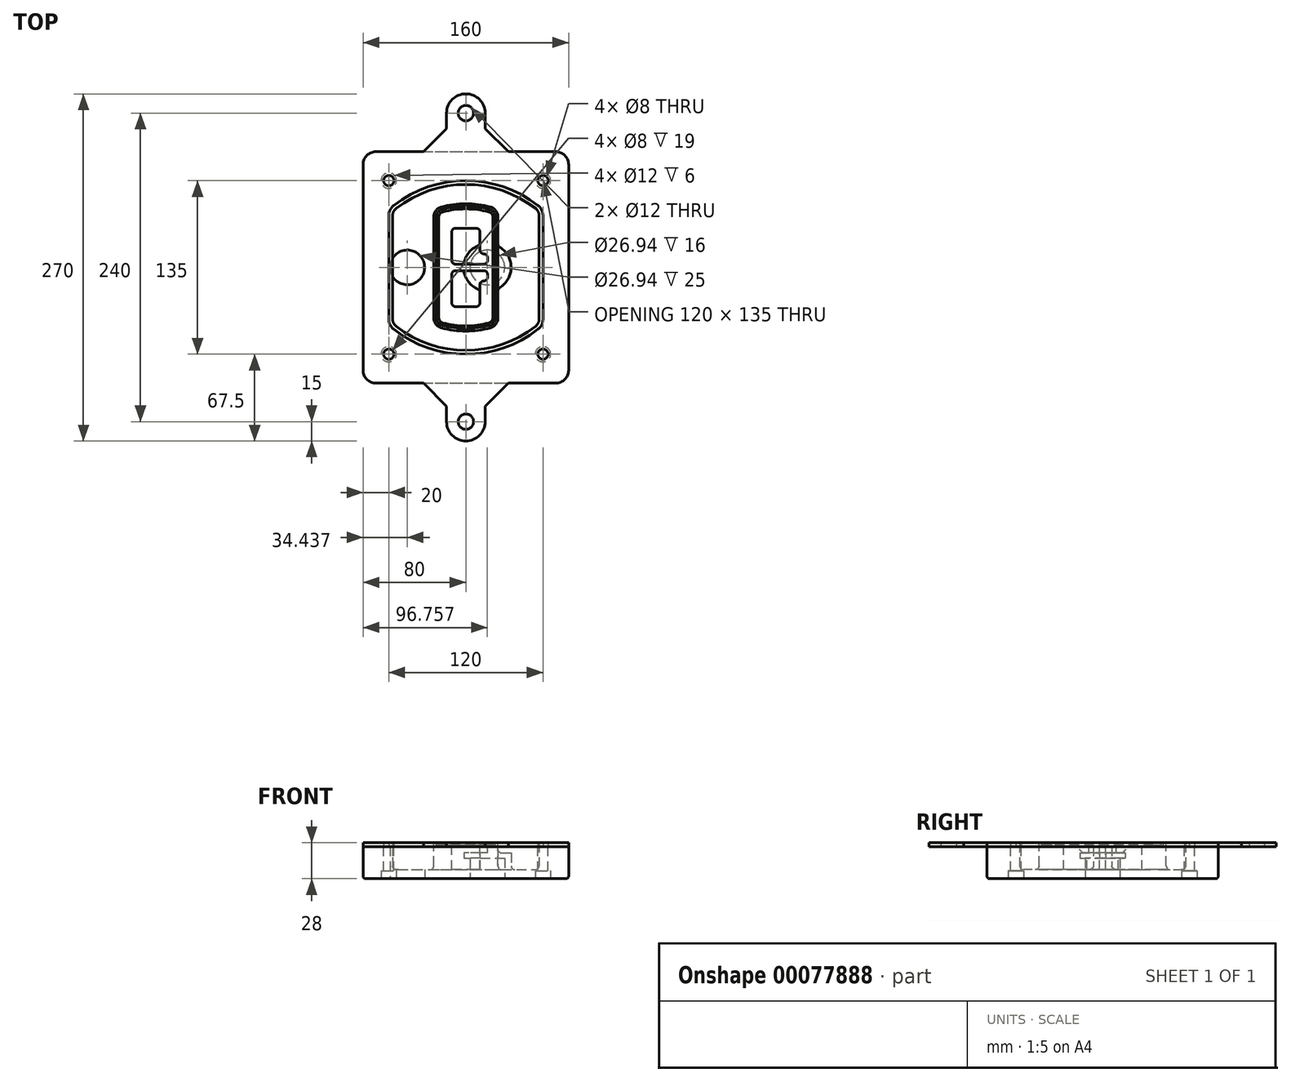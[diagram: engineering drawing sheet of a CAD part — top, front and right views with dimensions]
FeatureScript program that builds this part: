
annotation { "Feature Type Name" : "Feature", "Feature Type Description" : "" }
export const myFeature = defineFeature(function(context is Context, id is Id, definition is map)
    precondition{}
    {
        {
            var Q0;
            Q0=qCreatedBy(makeId("Top.planeOp"),FACE);
            var sketch = newSketch(context, id + "F0", { "sketchPlane" : qUnion([Q0])});
            skPoint(sketch, "E0.rect.middle", {"position": v(0, 0) * mm});
            skLineSegment(sketch, "E1.bottom", {"start": v(-70, -90) * mm, "end": v(70, -90) * mm});
            skLineSegment(sketch, "E1.top", {"start": v(-70, 90) * mm, "end": v(70, 90) * mm});
            skLineSegment(sketch, "E1.left", {"start": v(-80, -80) * mm, "end": v(-80, 80) * mm});
            skLineSegment(sketch, "E1.right", {"start": v(80, -80) * mm, "end": v(80, 80) * mm});
            skLineSegment(sketch, "E2", {"start": v(-80, 90) * mm, "end": v(80, -90) * mm, "construction": true});
            skLineSegment(sketch, "E3", {"start": v(80, 90) * mm, "end": v(-80, -90) * mm, "construction": true});
            skCircle(sketch, "E4", {"center": v(-60, 67.5) * mm, "radius": 4 * mm});
            skCircle(sketch, "E5", {"center": v(60, 67.5) * mm, "radius": 4 * mm});
            skCircle(sketch, "E6", {"center": v(60, -67.5) * mm, "radius": 4 * mm});
            skCircle(sketch, "E7", {"center": v(-60, -67.5) * mm, "radius": 4 * mm});
            skLineSegment(sketch, "E8", {"start": v(-60, 67.5) * mm, "end": v(60, 67.5) * mm, "construction": true});
            skLineSegment(sketch, "E9", {"start": v(60, 67.5) * mm, "end": v(60, -67.5) * mm, "construction": true});
            skLineSegment(sketch, "E10", {"start": v(60, -67.5) * mm, "end": v(-60, -67.5) * mm, "construction": true});
            skLineSegment(sketch, "E11", {"start": v(-60, -67.5) * mm, "end": v(-60, 67.5) * mm, "construction": true});
            skLineSegment(sketch, "E12", {"start": v(-60, 40.3) * mm, "end": v(-60, -40.3) * mm});
            skLineSegment(sketch, "E13", {"start": v(60, 40.3) * mm, "end": v(60, -40.3) * mm});
            skArc(sketch, "E14", {"start": v(56.15, 48.18) * mm, "mid": v(0, 67.5) * mm, "end": v(-56.15, 48.18) * mm});
            skArc(sketch, "E15", {"start": v(-56.15, -48.18) * mm, "mid": v(0, -67.5) * mm, "end": v(56.15, -48.18) * mm});
            skLineSegment(sketch, "E16", {"start": v(-60, 0) * mm, "end": v(60, 0) * mm, "construction": true});
            skPoint(sketch, "E17.visualSharp", {"position": v(-60, -45) * mm});
            skArc(sketch, "E17.filletArc", {"start": v(-60, -40.3) * mm, "mid": v(-58.99, -44.68) * mm, "end": v(-56.15, -48.18) * mm});
            skPoint(sketch, "E18.visualSharp", {"position": v(-60, 45) * mm});
            skArc(sketch, "E18.filletArc", {"start": v(-56.15, 48.18) * mm, "mid": v(-58.99, 44.68) * mm, "end": v(-60, 40.3) * mm});
            skPoint(sketch, "E19.visualSharp", {"position": v(60, 45) * mm});
            skArc(sketch, "E19.filletArc", {"start": v(60, 40.3) * mm, "mid": v(58.99, 44.68) * mm, "end": v(56.15, 48.18) * mm});
            skPoint(sketch, "E20.visualSharp", {"position": v(60, -45) * mm});
            skArc(sketch, "E20.filletArc", {"start": v(56.15, -48.18) * mm, "mid": v(58.99, -44.68) * mm, "end": v(60, -40.3) * mm});
            skPoint(sketch, "E21.visualSharp", {"position": v(-80, 90) * mm});
            skArc(sketch, "E21.filletArc", {"start": v(-70, 90) * mm, "mid": v(-77.07, 87.07) * mm, "end": v(-80, 80) * mm});
            skPoint(sketch, "E22.visualSharp", {"position": v(80, 90) * mm});
            skArc(sketch, "E22.filletArc", {"start": v(80, 80) * mm, "mid": v(77.07, 87.07) * mm, "end": v(70, 90) * mm});
            skPoint(sketch, "E23.visualSharp", {"position": v(80, -90) * mm});
            skArc(sketch, "E23.filletArc", {"start": v(70, -90) * mm, "mid": v(77.07, -87.07) * mm, "end": v(80, -80) * mm});
            skPoint(sketch, "E24.visualSharp", {"position": v(-80, -90) * mm});
            skArc(sketch, "E24.filletArc", {"start": v(-80, -80) * mm, "mid": v(-77.07, -87.07) * mm, "end": v(-70, -90) * mm});
            skArc(sketch, "E25.0", {"start": v(57, 40.3) * mm, "mid": v(56.3, 43.36) * mm, "end": v(54.3, 45.81) * mm});
            skLineSegment(sketch, "E25.1", {"start": v(57, 40.3) * mm, "end": v(57, -40.3) * mm});
            skArc(sketch, "E25.2", {"start": v(54.3, -45.81) * mm, "mid": v(56.3, -43.36) * mm, "end": v(57, -40.3) * mm});
            skArc(sketch, "E25.3", {"start": v(-54.3, -45.81) * mm, "mid": v(0, -64.5) * mm, "end": v(54.3, -45.81) * mm});
            skArc(sketch, "E25.4", {"start": v(-57, -40.3) * mm, "mid": v(-56.3, -43.36) * mm, "end": v(-54.3, -45.81) * mm});
            skArc(sketch, "E25.5", {"start": v(54.3, 45.81) * mm, "mid": v(0, 64.5) * mm, "end": v(-54.3, 45.81) * mm});
            skLineSegment(sketch, "E25.6", {"start": v(-57, 40.3) * mm, "end": v(-57, -40.3) * mm});
            skArc(sketch, "E25.7", {"start": v(-54.3, 45.81) * mm, "mid": v(-56.3, 43.36) * mm, "end": v(-57, 40.3) * mm});
            skArc(sketch, "E26.0", {"start": v(-58.62, 51.33) * mm, "mid": v(-62.58, 46.43) * mm, "end": v(-64, 40.3) * mm});
            skArc(sketch, "E26.1", {"start": v(58.62, 51.33) * mm, "mid": v(0, 71.5) * mm, "end": v(-58.62, 51.33) * mm});
            skArc(sketch, "E26.2", {"start": v(64, 40.3) * mm, "mid": v(62.58, 46.43) * mm, "end": v(58.62, 51.33) * mm});
            skLineSegment(sketch, "E26.3", {"start": v(64, 40.3) * mm, "end": v(64, -40.3) * mm});
            skArc(sketch, "E26.4", {"start": v(58.62, -51.33) * mm, "mid": v(62.58, -46.43) * mm, "end": v(64, -40.3) * mm});
            skLineSegment(sketch, "E26.5", {"start": v(-64, 40.3) * mm, "end": v(-64, -40.3) * mm});
            skArc(sketch, "E26.6", {"start": v(-58.62, -51.33) * mm, "mid": v(0, -71.5) * mm, "end": v(58.62, -51.33) * mm});
            skArc(sketch, "E26.7", {"start": v(-64, -40.3) * mm, "mid": v(-62.58, -46.43) * mm, "end": v(-58.62, -51.33) * mm});
            skSolve(sketch);
        }
        {
            var Q0;
            Q0=makeQuery(id+"F0.imprint","IMPRINT",FACE,{"disambiguationData":[TD([[makeQuery(id+"F0.imprint","IMPRINT",EDGE,{"derivedFrom":sQuery(id+"F0.wireOp",EDGE,"E1.bottom")}),1.0]])]});
            var Q1;
            Q1=makeQuery(id+"F0.imprint","IMPRINT",FACE,{"disambiguationData":[TD([[makeQuery(id+"F0.imprint","IMPRINT",EDGE,{"derivedFrom":sQuery(id+"F0.wireOp",EDGE,"E12")}),1.0]])]});
            var Q2;
            Q2=makeQuery(id+"F0.imprint","IMPRINT",FACE,{"disambiguationData":[TD([[makeQuery(id+"F0.imprint","IMPRINT",EDGE,{"derivedFrom":sQuery(id+"F0.wireOp",EDGE,"E25.0")}),1.0]])]});
            var Q3;
            Q3=makeQuery(id+"F0.imprint","IMPRINT",FACE,{"disambiguationData":[TD([[makeQuery(id+"F0.imprint","IMPRINT",EDGE,{"derivedFrom":sQuery(id+"F0.wireOp",EDGE,"E12")}),-1.0]])]});
            extrude(context, id + "F1", {"entities" : qUnion([Q0, Q1, Q2, Q3]), "oppositeDirection" : true, "depth" : 25 * mm});
        }
        {
            var Q0;
            Q0=makeQuery(id+"F0.imprint","IMPRINT",FACE,{"disambiguationData":[TD([[makeQuery(id+"F0.imprint","IMPRINT",EDGE,{"derivedFrom":sQuery(id+"F0.wireOp",EDGE,"E12")}),1.0]])]});
            extrude(context, id + "F2", {"entities" : qUnion([Q0]), "operationType" : NewBodyOperationType.ADD, "depth" : 3 * mm});
        }
        {
            var Q0;
            Q0=makeQuery(id+"F0.imprint","IMPRINT",FACE,{"disambiguationData":[TD([[makeQuery(id+"F0.imprint","IMPRINT",EDGE,{"derivedFrom":sQuery(id+"F0.wireOp",EDGE,"E25.0")}),1.0]])]});
            extrude(context, id + "F3", {"entities" : qUnion([Q0]), "operationType" : NewBodyOperationType.REMOVE, "oppositeDirection" : true, "depth" : 18 * mm});
        }
        {
            var Q0;
            Q0=makeQuery(id+"F2.opExtrude","CAP_FACE",FACE,{"disambiguationData":[OSD([sQuery(id+"F0.wireOp",EDGE,"E12"),sQuery(id+"F0.wireOp",EDGE,"E13"),sQuery(id+"F0.wireOp",EDGE,"E14"),sQuery(id+"F0.wireOp",EDGE,"E15"),sQuery(id+"F0.wireOp",EDGE,"E17.filletArc"),sQuery(id+"F0.wireOp",EDGE,"E18.filletArc"),sQuery(id+"F0.wireOp",EDGE,"E19.filletArc"),sQuery(id+"F0.wireOp",EDGE,"E20.filletArc"),sQuery(id+"F0.wireOp",EDGE,"E25.0"),sQuery(id+"F0.wireOp",EDGE,"E25.1"),sQuery(id+"F0.wireOp",EDGE,"E25.2"),sQuery(id+"F0.wireOp",EDGE,"E25.3"),sQuery(id+"F0.wireOp",EDGE,"E25.4"),sQuery(id+"F0.wireOp",EDGE,"E25.5"),sQuery(id+"F0.wireOp",EDGE,"E25.6"),sQuery(id+"F0.wireOp",EDGE,"E25.7")])],"isStart":false});
            var sketch = newSketch(context, id + "F4", { "sketchPlane" : qUnion([Q0])});
            skArc(sketch, "E27.0", {"start": v(-19.08, -46.97) * mm, "mid": v(0, -49.5) * mm, "end": v(19.08, -46.97) * mm});
            skArc(sketch, "E28.0", {"start": v(19.08, 46.97) * mm, "mid": v(0, 49.5) * mm, "end": v(-19.08, 46.97) * mm});
            skLineSegment(sketch, "E29", {"start": v(-25, 39.25) * mm, "end": v(-25, -39.25) * mm});
            skLineSegment(sketch, "E30", {"start": v(25, 39.25) * mm, "end": v(25, -39.25) * mm});
            skLineSegment(sketch, "E31", {"start": v(-25, 45.1) * mm, "end": v(25, 45.1) * mm, "construction": true});
            skLineSegment(sketch, "E32", {"start": v(-25, -45.1) * mm, "end": v(25, -45.1) * mm, "construction": true});
            skPoint(sketch, "E33.visualSharp", {"position": v(-25, 45.1) * mm});
            skArc(sketch, "E33.filletArc", {"start": v(-19.08, 46.97) * mm, "mid": v(-23.35, 44.11) * mm, "end": v(-25, 39.25) * mm});
            skPoint(sketch, "E34.visualSharp", {"position": v(25, 45.1) * mm});
            skArc(sketch, "E34.filletArc", {"start": v(25, 39.25) * mm, "mid": v(23.35, 44.11) * mm, "end": v(19.08, 46.97) * mm});
            skPoint(sketch, "E35.visualSharp", {"position": v(25, -45.1) * mm});
            skArc(sketch, "E35.filletArc", {"start": v(19.08, -46.97) * mm, "mid": v(23.35, -44.11) * mm, "end": v(25, -39.25) * mm});
            skPoint(sketch, "E36.visualSharp", {"position": v(-25, -45.1) * mm});
            skArc(sketch, "E36.filletArc", {"start": v(-25, -39.25) * mm, "mid": v(-23.35, -44.11) * mm, "end": v(-19.08, -46.97) * mm});
            skArc(sketch, "E37.0", {"start": v(54.3, 45.81) * mm, "mid": v(0, 64.5) * mm, "end": v(-54.3, 45.81) * mm});
            skArc(sketch, "E37.1", {"start": v(-54.3, 45.81) * mm, "mid": v(-56.3, 43.36) * mm, "end": v(-57, 40.3) * mm});
            skLineSegment(sketch, "E37.2", {"start": v(-57, 40.3) * mm, "end": v(-57, -40.3) * mm});
            skArc(sketch, "E37.3", {"start": v(-57, -40.3) * mm, "mid": v(-56.3, -43.36) * mm, "end": v(-54.3, -45.81) * mm});
            skArc(sketch, "E37.4", {"start": v(-54.3, -45.81) * mm, "mid": v(0, -64.5) * mm, "end": v(54.3, -45.81) * mm});
            skArc(sketch, "E37.5", {"start": v(54.3, -45.81) * mm, "mid": v(56.3, -43.36) * mm, "end": v(57, -40.3) * mm});
            skLineSegment(sketch, "E37.6", {"start": v(57, 40.3) * mm, "end": v(57, -40.3) * mm});
            skArc(sketch, "E37.7", {"start": v(57, 40.3) * mm, "mid": v(56.3, 43.36) * mm, "end": v(54.3, 45.81) * mm});
            skLineSegment(sketch, "E38.0", {"start": v(23, 39.25) * mm, "end": v(23, -39.25) * mm});
            skArc(sketch, "E38.1", {"start": v(18.56, -45.04) * mm, "mid": v(21.76, -42.9) * mm, "end": v(23, -39.25) * mm});
            skArc(sketch, "E38.2", {"start": v(-18.56, -45.04) * mm, "mid": v(0, -47.5) * mm, "end": v(18.56, -45.04) * mm});
            skArc(sketch, "E38.3", {"start": v(-23, -39.25) * mm, "mid": v(-21.76, -42.9) * mm, "end": v(-18.56, -45.04) * mm});
            skLineSegment(sketch, "E38.4", {"start": v(-23, 39.25) * mm, "end": v(-23, -39.25) * mm});
            skArc(sketch, "E38.5", {"start": v(23, 39.25) * mm, "mid": v(21.76, 42.9) * mm, "end": v(18.56, 45.04) * mm});
            skArc(sketch, "E38.6", {"start": v(-18.56, 45.04) * mm, "mid": v(-21.76, 42.9) * mm, "end": v(-23, 39.25) * mm});
            skArc(sketch, "E38.7", {"start": v(18.56, 45.04) * mm, "mid": v(0, 47.5) * mm, "end": v(-18.56, 45.04) * mm});
            skArc(sketch, "E39.0", {"start": v(21, 39.25) * mm, "mid": v(20.18, 41.68) * mm, "end": v(18.04, 43.1) * mm});
            skLineSegment(sketch, "E39.1", {"start": v(21, 39.25) * mm, "end": v(21, -39.25) * mm});
            skArc(sketch, "E39.2", {"start": v(18.04, -43.1) * mm, "mid": v(20.18, -41.68) * mm, "end": v(21, -39.25) * mm});
            skArc(sketch, "E39.3", {"start": v(-18.04, -43.1) * mm, "mid": v(0, -45.5) * mm, "end": v(18.04, -43.1) * mm});
            skArc(sketch, "E39.4", {"start": v(-21, -39.25) * mm, "mid": v(-20.18, -41.68) * mm, "end": v(-18.04, -43.1) * mm});
            skArc(sketch, "E39.5", {"start": v(18.04, 43.1) * mm, "mid": v(0, 45.5) * mm, "end": v(-18.04, 43.1) * mm});
            skLineSegment(sketch, "E39.6", {"start": v(-21, 39.25) * mm, "end": v(-21, -39.25) * mm});
            skArc(sketch, "E39.7", {"start": v(-18.04, 43.1) * mm, "mid": v(-20.18, 41.68) * mm, "end": v(-21, 39.25) * mm});
            skLineSegment(sketch, "E40", {"start": v(-25, 0) * mm, "end": v(25, 0) * mm, "construction": true});
            skLineSegment(sketch, "E41", {"start": v(-11, 5.5) * mm, "end": v(-11, 27.5) * mm});
            skLineSegment(sketch, "E42", {"start": v(-8, 30.5) * mm, "end": v(8, 30.5) * mm});
            skLineSegment(sketch, "E43", {"start": v(11, 27.5) * mm, "end": v(11, 13.5) * mm});
            skLineSegment(sketch, "E44", {"start": v(14, 10.5) * mm, "end": v(14, 10.5) * mm});
            skLineSegment(sketch, "E45", {"start": v(17, 7.5) * mm, "end": v(17, 5.5) * mm});
            skLineSegment(sketch, "E46", {"start": v(14, 2.5) * mm, "end": v(-8, 2.5) * mm});
            skPoint(sketch, "E47.visualSharp", {"position": v(-11, 30.5) * mm});
            skArc(sketch, "E47.filletArc", {"start": v(-8, 30.5) * mm, "mid": v(-10.12, 29.62) * mm, "end": v(-11, 27.5) * mm});
            skPoint(sketch, "E48.visualSharp", {"position": v(11, 30.5) * mm});
            skArc(sketch, "E48.filletArc", {"start": v(11, 27.5) * mm, "mid": v(10.12, 29.62) * mm, "end": v(8, 30.5) * mm});
            skPoint(sketch, "E49.visualSharp", {"position": v(11, 10.5) * mm});
            skArc(sketch, "E49.filletArc", {"start": v(11, 13.5) * mm, "mid": v(11.88, 11.38) * mm, "end": v(14, 10.5) * mm});
            skPoint(sketch, "E50.visualSharp", {"position": v(17, 10.5) * mm});
            skArc(sketch, "E50.filletArc", {"start": v(17, 7.5) * mm, "mid": v(16.12, 9.62) * mm, "end": v(14, 10.5) * mm});
            skPoint(sketch, "E51.visualSharp", {"position": v(17, 2.5) * mm});
            skArc(sketch, "E51.filletArc", {"start": v(14, 2.5) * mm, "mid": v(16.12, 3.38) * mm, "end": v(17, 5.5) * mm});
            skPoint(sketch, "E52.visualSharp", {"position": v(-11, 2.5) * mm});
            skArc(sketch, "E52.filletArc", {"start": v(-11, 5.5) * mm, "mid": v(-10.12, 3.38) * mm, "end": v(-8, 2.5) * mm});
            skLineSegment(sketch, "E53.0.MirrorCS", {"start": v(14, -2.5) * mm, "end": v(-8, -2.5) * mm});
            skArc(sketch, "E54.0.MirrorCS", {"start": v(-11, -5.5) * mm, "mid": v(-10.12, -3.38) * mm, "end": v(-8, -2.5) * mm});
            skLineSegment(sketch, "E55.0.MirrorCS", {"start": v(-11, -5.5) * mm, "end": v(-11, -27.5) * mm});
            skArc(sketch, "E56.0.MirrorCS", {"start": v(-8, -30.5) * mm, "mid": v(-10.12, -29.62) * mm, "end": v(-11, -27.5) * mm});
            skLineSegment(sketch, "E57.0.MirrorCS", {"start": v(-8, -30.5) * mm, "end": v(8, -30.5) * mm});
            skArc(sketch, "E58.0.MirrorCS", {"start": v(11, -27.5) * mm, "mid": v(10.12, -29.62) * mm, "end": v(8, -30.5) * mm});
            skLineSegment(sketch, "E59.0.MirrorCS", {"start": v(11, -27.5) * mm, "end": v(11, -13.5) * mm});
            skArc(sketch, "E60.0.MirrorCS", {"start": v(11, -13.5) * mm, "mid": v(11.88, -11.38) * mm, "end": v(14, -10.5) * mm});
            skArc(sketch, "E61.0.MirrorCS", {"start": v(17, -7.5) * mm, "mid": v(16.12, -9.62) * mm, "end": v(14, -10.5) * mm});
            skLineSegment(sketch, "E62.0.MirrorCS", {"start": v(17, -7.5) * mm, "end": v(17, -5.5) * mm});
            skArc(sketch, "E63.0.MirrorCS", {"start": v(14, -2.5) * mm, "mid": v(16.12, -3.38) * mm, "end": v(17, -5.5) * mm});
            skSolve(sketch);
        }
        {
            var Q0;
            Q0=makeQuery(id+"F4.imprint","IMPRINT",FACE,{"disambiguationData":[TD([[makeQuery(id+"F4.imprint","IMPRINT",EDGE,{"derivedFrom":sQuery(id+"F4.wireOp",EDGE,"E27.0")}),1.0]])]});
            var Q1;
            Q1=makeQuery(id+"F4.imprint","IMPRINT",FACE,{"disambiguationData":[TD([[makeQuery(id+"F4.imprint","IMPRINT",EDGE,{"derivedFrom":sQuery(id+"F4.wireOp",EDGE,"E38.0")}),-1.0]])]});
            var Q2;
            Q2=makeQuery(id+"F4.imprint","IMPRINT",FACE,{"disambiguationData":[TD([[makeQuery(id+"F4.imprint","IMPRINT",EDGE,{"derivedFrom":sQuery(id+"F4.wireOp",EDGE,"E39.0")}),1.0]])]});
            extrude(context, id + "F5", {"entities" : qUnion([Q0, Q1, Q2]), "operationType" : NewBodyOperationType.ADD, "endBound" : BoundingType.UP_TO_NEXT, "oppositeDirection" : true, "depth" : 25 * mm});
        }
        {
            var Q0;
            Q0=makeQuery(id+"F4.imprint","IMPRINT",FACE,{"disambiguationData":[TD([[makeQuery(id+"F4.imprint","IMPRINT",EDGE,{"derivedFrom":sQuery(id+"F4.wireOp",EDGE,"E38.0")}),-1.0]])]});
            extrude(context, id + "F6", {"entities" : qUnion([Q0]), "operationType" : NewBodyOperationType.REMOVE, "oppositeDirection" : true, "depth" : 2 * mm});
        }
        {
            var Q0;
            Q0=makeQuery(id+"F1.opExtrude","CAP_FACE",FACE,{"disambiguationData":[OSD([sQuery(id+"F0.wireOp",EDGE,"E1.bottom"),sQuery(id+"F0.wireOp",EDGE,"E1.top"),sQuery(id+"F0.wireOp",EDGE,"E1.left"),sQuery(id+"F0.wireOp",EDGE,"E1.right"),sQuery(id+"F0.wireOp",EDGE,"E4"),sQuery(id+"F0.wireOp",EDGE,"E5"),sQuery(id+"F0.wireOp",EDGE,"E6"),sQuery(id+"F0.wireOp",EDGE,"E7"),sQuery(id+"F0.wireOp",EDGE,"E21.filletArc"),sQuery(id+"F0.wireOp",EDGE,"E22.filletArc"),sQuery(id+"F0.wireOp",EDGE,"E23.filletArc"),sQuery(id+"F0.wireOp",EDGE,"E24.filletArc")])],"isStart":false});
            var sketch = newSketch(context, id + "F7", { "sketchPlane" : qUnion([Q0])});
            skCircle(sketch, "E64", {"center": v(16.76, 0) * mm, "radius": 13.47 * mm});
            skCircle(sketch, "E65", {"center": v(-45.56, 0) * mm, "radius": 13.47 * mm});
            skLineSegment(sketch, "E66", {"start": v(80, 0) * mm, "end": v(-80, 0) * mm});
            skCircle(sketch, "E67", {"center": v(16.76, 0) * mm, "radius": 18.47 * mm});
            skCircle(sketch, "E68", {"center": v(60, -67.5) * mm, "radius": 6 * mm});
            skCircle(sketch, "E69", {"center": v(-60, -67.5) * mm, "radius": 6 * mm});
            skCircle(sketch, "E70", {"center": v(-60, 67.5) * mm, "radius": 6 * mm});
            skCircle(sketch, "E71", {"center": v(60, 67.5) * mm, "radius": 6 * mm});
            skSolve(sketch);
        }
        {
            var Q0;
            {var subQ1=sQuery(id+"F7.wireOp",EDGE,"E66");var subQ4=sQuery(id+"F7.wireOp",EDGE,"E64");var subQ6=makeQuery(id+"F7.imprint","INTERSECT",VERTEX,{"disambiguationData":[OD(0.0)],"derivedFrom":[subQ4,subQ1]});Q0=makeQuery(id+"F7.imprint","IMPRINT",FACE,{"disambiguationData":[TD([[makeQuery(id+"F7.imprint","IMPRINT",EDGE,{"disambiguationData":[TD([[subQ6,-1.0]])],"derivedFrom":subQ4}),-1.0]])]});}
            var Q1;
            {var subQ0=sQuery(id+"F7.wireOp",EDGE,"E66");var subQ1=sQuery(id+"F7.wireOp",EDGE,"E64");var subQ3=makeQuery(id+"F7.imprint","INTERSECT",VERTEX,{"disambiguationData":[OD(0.0)],"derivedFrom":[subQ1,subQ0]});Q1=makeQuery(id+"F7.imprint","IMPRINT",FACE,{"disambiguationData":[TD([[makeQuery(id+"F7.imprint","IMPRINT",EDGE,{"disambiguationData":[TD([[subQ3,-1.0]])],"derivedFrom":subQ1}),1.0]])]});}
            var Q2;
            {var subQ0=sQuery(id+"F7.wireOp",EDGE,"E66");var subQ1=sQuery(id+"F7.wireOp",EDGE,"E64");var subQ3=makeQuery(id+"F7.imprint","INTERSECT",VERTEX,{"disambiguationData":[OD(0.0)],"derivedFrom":[subQ1,subQ0]});Q2=makeQuery(id+"F7.imprint","IMPRINT",FACE,{"disambiguationData":[TD([[makeQuery(id+"F7.imprint","IMPRINT",EDGE,{"disambiguationData":[TD([[subQ3,1.0]])],"derivedFrom":subQ1}),1.0]])]});}
            var Q3;
            {var subQ1=sQuery(id+"F7.wireOp",EDGE,"E66");var subQ4=sQuery(id+"F7.wireOp",EDGE,"E64");var subQ6=makeQuery(id+"F7.imprint","INTERSECT",VERTEX,{"disambiguationData":[OD(0.0)],"derivedFrom":[subQ4,subQ1]});Q3=makeQuery(id+"F7.imprint","IMPRINT",FACE,{"disambiguationData":[TD([[makeQuery(id+"F7.imprint","IMPRINT",EDGE,{"disambiguationData":[TD([[subQ6,1.0]])],"derivedFrom":subQ4}),-1.0]])]});}
            extrude(context, id + "F8", {"entities" : qUnion([Q0, Q1, Q2, Q3]), "operationType" : NewBodyOperationType.ADD, "oppositeDirection" : true, "depth" : 20 * mm});
        }
        {
            var Q0;
            {var subQ0=sQuery(id+"F7.wireOp",EDGE,"E66");var subQ1=sQuery(id+"F7.wireOp",EDGE,"E64");var subQ3=makeQuery(id+"F7.imprint","INTERSECT",VERTEX,{"disambiguationData":[OD(0.0)],"derivedFrom":[subQ1,subQ0]});Q0=makeQuery(id+"F7.imprint","IMPRINT",FACE,{"disambiguationData":[TD([[makeQuery(id+"F7.imprint","IMPRINT",EDGE,{"disambiguationData":[TD([[subQ3,-1.0]])],"derivedFrom":subQ1}),1.0]])]});}
            var Q1;
            {var subQ0=sQuery(id+"F7.wireOp",EDGE,"E66");var subQ1=sQuery(id+"F7.wireOp",EDGE,"E64");var subQ3=makeQuery(id+"F7.imprint","INTERSECT",VERTEX,{"disambiguationData":[OD(0.0)],"derivedFrom":[subQ1,subQ0]});Q1=makeQuery(id+"F7.imprint","IMPRINT",FACE,{"disambiguationData":[TD([[makeQuery(id+"F7.imprint","IMPRINT",EDGE,{"disambiguationData":[TD([[subQ3,1.0]])],"derivedFrom":subQ1}),1.0]])]});}
            extrude(context, id + "F9", {"entities" : qUnion([Q0, Q1]), "operationType" : NewBodyOperationType.REMOVE, "oppositeDirection" : true, "depth" : 16 * mm});
        }
        {
            var Q0;
            {var subQ0=sQuery(id+"F7.wireOp",EDGE,"E66");var subQ1=sQuery(id+"F7.wireOp",EDGE,"E65");var subQ3=makeQuery(id+"F7.imprint","INTERSECT",VERTEX,{"disambiguationData":[OD(0.0)],"derivedFrom":[subQ1,subQ0]});Q0=makeQuery(id+"F7.imprint","IMPRINT",FACE,{"disambiguationData":[TD([[makeQuery(id+"F7.imprint","IMPRINT",EDGE,{"disambiguationData":[TD([[subQ3,-1.0]])],"derivedFrom":subQ1}),1.0]])]});}
            var Q1;
            {var subQ0=sQuery(id+"F7.wireOp",EDGE,"E66");var subQ1=sQuery(id+"F7.wireOp",EDGE,"E65");var subQ3=makeQuery(id+"F7.imprint","INTERSECT",VERTEX,{"disambiguationData":[OD(0.0)],"derivedFrom":[subQ1,subQ0]});Q1=makeQuery(id+"F7.imprint","IMPRINT",FACE,{"disambiguationData":[TD([[makeQuery(id+"F7.imprint","IMPRINT",EDGE,{"disambiguationData":[TD([[subQ3,1.0]])],"derivedFrom":subQ1}),1.0]])]});}
            extrude(context, id + "F10", {"entities" : qUnion([Q0, Q1]), "operationType" : NewBodyOperationType.REMOVE, "oppositeDirection" : true, "depth" : 25 * mm});
        }
        {
            var Q0;
            Q0=makeQuery(id+"F7.imprint","IMPRINT",FACE,{"disambiguationData":[TD([[makeQuery(id+"F7.imprint","IMPRINT",EDGE,{"derivedFrom":sQuery(id+"F7.wireOp",EDGE,"E68")}),1.0]])]});
            var Q1;
            Q1=makeQuery(id+"F7.imprint","IMPRINT",FACE,{"disambiguationData":[TD([[makeQuery(id+"F7.imprint","IMPRINT",EDGE,{"derivedFrom":makeQuery(id+"F1.opExtrude","CAP_EDGE",EDGE,{"disambiguationData":[OSD([sQuery(id+"F0.wireOp",EDGE,"E5")])],"isStart":false})}),-1.0]])]});
            var Q2;
            Q2=makeQuery(id+"F7.imprint","IMPRINT",FACE,{"disambiguationData":[TD([[makeQuery(id+"F7.imprint","IMPRINT",EDGE,{"derivedFrom":sQuery(id+"F7.wireOp",EDGE,"E69")}),1.0]])]});
            var Q3;
            Q3=makeQuery(id+"F7.imprint","IMPRINT",FACE,{"disambiguationData":[TD([[makeQuery(id+"F7.imprint","IMPRINT",EDGE,{"derivedFrom":makeQuery(id+"F1.opExtrude","CAP_EDGE",EDGE,{"disambiguationData":[OSD([sQuery(id+"F0.wireOp",EDGE,"E4")])],"isStart":false})}),-1.0]])]});
            var Q4;
            Q4=makeQuery(id+"F7.imprint","IMPRINT",FACE,{"disambiguationData":[TD([[makeQuery(id+"F7.imprint","IMPRINT",EDGE,{"derivedFrom":sQuery(id+"F7.wireOp",EDGE,"E70")}),1.0]])]});
            var Q5;
            Q5=makeQuery(id+"F7.imprint","IMPRINT",FACE,{"disambiguationData":[TD([[makeQuery(id+"F7.imprint","IMPRINT",EDGE,{"derivedFrom":makeQuery(id+"F1.opExtrude","CAP_EDGE",EDGE,{"disambiguationData":[OSD([sQuery(id+"F0.wireOp",EDGE,"E7")])],"isStart":false})}),-1.0]])]});
            var Q6;
            Q6=makeQuery(id+"F7.imprint","IMPRINT",FACE,{"disambiguationData":[TD([[makeQuery(id+"F7.imprint","IMPRINT",EDGE,{"derivedFrom":sQuery(id+"F7.wireOp",EDGE,"E71")}),1.0]])]});
            var Q7;
            Q7=makeQuery(id+"F7.imprint","IMPRINT",FACE,{"disambiguationData":[TD([[makeQuery(id+"F7.imprint","IMPRINT",EDGE,{"derivedFrom":makeQuery(id+"F1.opExtrude","CAP_EDGE",EDGE,{"disambiguationData":[OSD([sQuery(id+"F0.wireOp",EDGE,"E6")])],"isStart":false})}),-1.0]])]});
            extrude(context, id + "F11", {"entities" : qUnion([Q0, Q1, Q2, Q3, Q4, Q5, Q6, Q7]), "operationType" : NewBodyOperationType.REMOVE, "oppositeDirection" : true, "depth" : 6 * mm});
        }
        {
            var Q0;
            Q0=makeQuery(id+"F9.boolean.opBoolean","COPY",FACE,{"derivedFrom":makeQuery(id+"F9.opExtrude","CAP_FACE",FACE,{"disambiguationData":[OSD([sQuery(id+"F7.wireOp",EDGE,"E64")])],"isStart":false})});
            var sketch = newSketch(context, id + "F12", { "sketchPlane" : qUnion([Q0])});
            skArc(sketch, "E72.0", {"start": v(11, 17.55) * mm, "mid": v(2.57, 11.82) * mm, "end": v(-1.54, 2.5) * mm});
            skArc(sketch, "E72.1", {"start": v(-1.54, -2.5) * mm, "mid": v(2.57, -11.82) * mm, "end": v(11, -17.55) * mm});
            skLineSegment(sketch, "E73", {"start": v(-1.54, -2.5) * mm, "end": v(14, -2.5) * mm});
            skLineSegment(sketch, "E74.0", {"start": v(14, 2.5) * mm, "end": v(-1.54, 2.5) * mm});
            skArc(sketch, "E74.1", {"start": v(14, 2.5) * mm, "mid": v(16.12, 3.38) * mm, "end": v(17, 5.5) * mm});
            skLineSegment(sketch, "E74.2", {"start": v(17, 7.5) * mm, "end": v(17, 5.5) * mm});
            skArc(sketch, "E74.3", {"start": v(17, 7.5) * mm, "mid": v(16.12, 9.62) * mm, "end": v(14, 10.5) * mm});
            skArc(sketch, "E74.4", {"start": v(11, 13.5) * mm, "mid": v(11.88, 11.38) * mm, "end": v(14, 10.5) * mm});
            skLineSegment(sketch, "E74.5", {"start": v(11, 17.55) * mm, "end": v(11, 13.5) * mm});
            skLineSegment(sketch, "E74.7", {"start": v(14, -2.5) * mm, "end": v(-1.54, -2.5) * mm});
            skArc(sketch, "E74.8", {"start": v(14, -2.5) * mm, "mid": v(16.12, -3.38) * mm, "end": v(17, -5.5) * mm});
            skLineSegment(sketch, "E74.9", {"start": v(17, -7.5) * mm, "end": v(17, -5.5) * mm});
            skArc(sketch, "E74.10", {"start": v(17, -7.5) * mm, "mid": v(16.12, -9.62) * mm, "end": v(14, -10.5) * mm});
            skArc(sketch, "E74.11", {"start": v(11, -13.5) * mm, "mid": v(11.88, -11.38) * mm, "end": v(14, -10.5) * mm});
            skLineSegment(sketch, "E74.12", {"start": v(11, -17.55) * mm, "end": v(11, -13.5) * mm});
            skPoint(sketch, "E75.orphan", {"position": v(11, -27.5) * mm});
            skPoint(sketch, "E76.orphan", {"position": v(-8, -2.5) * mm});
            skPoint(sketch, "E77.orphan", {"position": v(-8, 2.5) * mm});
            skPoint(sketch, "E78.orphan", {"position": v(11, 27.5) * mm});
            skSolve(sketch);
        }
        {
            var Q0;
            {var subQ7=sQuery(id+"F12.wireOp",EDGE,"E72.0");var subQ14=sQuery(id+"F12.wireOp",EDGE,"E72.1");var subQ16=sQuery(id+"F12.wireOp",EDGE,"E74.1");var subQ18=sQuery(id+"F12.wireOp",EDGE,"E74.8");Q0=qUnion([makeQuery(id+"F12.imprint","IMPRINT",FACE,{"disambiguationData":[TD([[makeQuery(id+"F12.imprint","IMPRINT",EDGE,{"derivedFrom":subQ7}),1.0]])]}),makeQuery(id+"F12.imprint","IMPRINT",FACE,{"disambiguationData":[TD([[makeQuery(id+"F12.imprint","IMPRINT",EDGE,{"derivedFrom":subQ14}),1.0]])]}),makeQuery(id+"F12.imprint","IMPRINT",FACE,{"disambiguationData":[TD([[makeQuery(id+"F12.imprint","IMPRINT",EDGE,{"derivedFrom":subQ16}),1.0]])]}),makeQuery(id+"F12.imprint","IMPRINT",FACE,{"disambiguationData":[TD([[makeQuery(id+"F12.imprint","IMPRINT",EDGE,{"derivedFrom":subQ18}),-1.0]])]})]);}
            var Q1;
            Q1=makeQuery(id+"F5.boolean.opBoolean","SPLIT",FACE,{"disambiguationData":[TD([makeQuery(id+"F5.opExtrude","SWEPT_FACE",FACE,{"disambiguationData":[OSD([sQuery(id+"F4.wireOp",EDGE,"E41")])]})])],"derivedFrom":makeQuery(id+"F3.boolean.opBoolean","COPY",FACE,{"derivedFrom":makeQuery(id+"F3.opExtrude","CAP_FACE",FACE,{"disambiguationData":[OSD([sQuery(id+"F0.wireOp",EDGE,"E25.0"),sQuery(id+"F0.wireOp",EDGE,"E25.1"),sQuery(id+"F0.wireOp",EDGE,"E25.2"),sQuery(id+"F0.wireOp",EDGE,"E25.3"),sQuery(id+"F0.wireOp",EDGE,"E25.4"),sQuery(id+"F0.wireOp",EDGE,"E25.5"),sQuery(id+"F0.wireOp",EDGE,"E25.6"),sQuery(id+"F0.wireOp",EDGE,"E25.7")])],"isStart":false})})});
            extrude(context, id + "F13", {"entities" : qUnion([Q0]), "operationType" : NewBodyOperationType.REMOVE, "endBound" : BoundingType.UP_TO_SURFACE, "endBoundEntityFace" : qUnion([Q1]), "depth" : 25 * mm});
        }
        {
            var Q0;
            Q0=makeQuery(id+"F3.boolean.opBoolean","COPY",EDGE,{"derivedFrom":makeQuery(id+"F3.opExtrude","CAP_EDGE",EDGE,{"disambiguationData":[OSD([sQuery(id+"F0.wireOp",EDGE,"E25.6")])],"isStart":false})});
            var Q1;
            Q1=makeQuery(id+"F8.boolean.opBoolean","INTERSECT",EDGE,{"derivedFrom":[makeQuery(id+"F5.opExtrude","SWEPT_FACE",FACE,{"disambiguationData":[OSD([sQuery(id+"F4.wireOp",EDGE,"E30")])]}),makeQuery(id+"F8.opExtrude","CAP_FACE",FACE,{"disambiguationData":[OSD([sQuery(id+"F7.wireOp",EDGE,"E67")])],"isStart":false})]});
            var Q2;
            Q2=makeQuery(id+"F8.boolean.opBoolean","INTERSECT",EDGE,{"disambiguationData":[OD(1.0)],"derivedFrom":[makeQuery(id+"F5.opExtrude","SWEPT_FACE",FACE,{"disambiguationData":[OSD([sQuery(id+"F4.wireOp",EDGE,"E30")])]}),makeQuery(id+"F8.opExtrude","SWEPT_FACE",FACE,{"disambiguationData":[OSD([sQuery(id+"F7.wireOp",EDGE,"E67")])]})]});
            var Q3;
            {var subQ0=sQuery(id+"F4.wireOp",EDGE,"E30");Q3=makeQuery(id+"F8.boolean.opBoolean","SPLIT",EDGE,{"disambiguationData":[TD([makeQuery(id+"F5.opExtrude","SWEPT_FACE",FACE,{"disambiguationData":[OSD([sQuery(id+"F4.wireOp",EDGE,"E35.filletArc")])]})])],"derivedFrom":makeQuery(id+"F5.opExtrude","CAP_EDGE",EDGE,{"disambiguationData":[OSD([subQ0])],"isStart":false})});}
            var Q4;
            {var subQ0=sQuery(id+"F0.wireOp",EDGE,"E25.7");var subQ1=sQuery(id+"F0.wireOp",EDGE,"E25.1");var subQ2=sQuery(id+"F0.wireOp",EDGE,"E25.6");var subQ3=sQuery(id+"F0.wireOp",EDGE,"E25.5");var subQ4=sQuery(id+"F0.wireOp",EDGE,"E25.4");var subQ5=sQuery(id+"F0.wireOp",EDGE,"E25.0");var subQ6=sQuery(id+"F0.wireOp",EDGE,"E25.2");var subQ7=sQuery(id+"F0.wireOp",EDGE,"E25.3");Q4=makeQuery(id+"F8.boolean.opBoolean","INTERSECT",EDGE,{"derivedFrom":[makeQuery(id+"F5.boolean.opBoolean","SPLIT",FACE,{"disambiguationData":[TD([makeQuery(id+"F2.opExtrude","SWEPT_FACE",FACE,{"disambiguationData":[OSD([subQ5])]})])],"derivedFrom":makeQuery(id+"F3.boolean.opBoolean","COPY",FACE,{"derivedFrom":makeQuery(id+"F3.opExtrude","CAP_FACE",FACE,{"disambiguationData":[OSD([subQ5,subQ1,subQ6,subQ7,subQ4,subQ3,subQ2,subQ0])],"isStart":false})})}),makeQuery(id+"F8.opExtrude","SWEPT_FACE",FACE,{"disambiguationData":[OSD([sQuery(id+"F7.wireOp",EDGE,"E67")])]})]});}
            var Q5;
            Q5=makeQuery(id+"F8.boolean.opBoolean","INTERSECT",EDGE,{"disambiguationData":[OD(0.0)],"derivedFrom":[makeQuery(id+"F5.opExtrude","SWEPT_FACE",FACE,{"disambiguationData":[OSD([sQuery(id+"F4.wireOp",EDGE,"E30")])]}),makeQuery(id+"F8.opExtrude","SWEPT_FACE",FACE,{"disambiguationData":[OSD([sQuery(id+"F7.wireOp",EDGE,"E67")])]})]});
            fillet(context, id + "F14", {"entities" : qUnion([Q0, Q1, Q2, Q3, Q4, Q5]), "radius" : 3 * mm, "tangentPropagation" : true, "allowEdgeOverflow" : false});
        }
        {
            var Q0;
            Q0=makeQuery(id+"F1.opExtrude","CAP_EDGE",EDGE,{"disambiguationData":[OSD([sQuery(id+"F0.wireOp",EDGE,"E1.bottom")])],"isStart":false});
            fillet(context, id + "F15", {"entities" : qUnion([Q0]), "radius" : 2 * mm, "tangentPropagation" : true, "allowEdgeOverflow" : false});
        }
        {
            var Q0;
            {var subQ0=sQuery(id+"F0.wireOp",EDGE,"E22.filletArc");var subQ1=sQuery(id+"F0.wireOp",EDGE,"E7");var subQ2=sQuery(id+"F0.wireOp",EDGE,"E6");var subQ3=sQuery(id+"F0.wireOp",EDGE,"E5");var subQ4=sQuery(id+"F0.wireOp",EDGE,"E4");var subQ5=sQuery(id+"F0.wireOp",EDGE,"E1.bottom");var subQ6=sQuery(id+"F0.wireOp",EDGE,"E21.filletArc");var subQ7=sQuery(id+"F0.wireOp",EDGE,"E1.top");var subQ8=sQuery(id+"F0.wireOp",EDGE,"E1.left");var subQ9=sQuery(id+"F0.wireOp",EDGE,"E1.right");var subQ10=sQuery(id+"F0.wireOp",EDGE,"E23.filletArc");var subQ11=sQuery(id+"F0.wireOp",EDGE,"E24.filletArc");Q0=makeQuery(id+"F2.boolean.opBoolean","SPLIT",FACE,{"disambiguationData":[TD([makeQuery(id+"F1.opExtrude","SWEPT_FACE",FACE,{"disambiguationData":[OSD([subQ5])]})])],"derivedFrom":makeQuery(id+"F1.opExtrude","CAP_FACE",FACE,{"disambiguationData":[OSD([subQ5,subQ7,subQ8,subQ9,subQ4,subQ3,subQ2,subQ1,subQ6,subQ0,subQ10,subQ11])],"isStart":true})});}
            var sketch = newSketch(context, id + "F16", { "sketchPlane" : qUnion([Q0])});
            skCircle(sketch, "E79.0", {"center": v(-60, 67.5) * mm, "radius": 4 * mm});
            skArc(sketch, "E79.1", {"start": v(-70, 90) * mm, "mid": v(-77.07, 87.07) * mm, "end": v(-80, 80) * mm});
            skLineSegment(sketch, "E79.2", {"start": v(-70, 90) * mm, "end": v(70, 90) * mm});
            skLineSegment(sketch, "E79.3", {"start": v(-80, -80) * mm, "end": v(-80, 80) * mm});
            skArc(sketch, "E79.4", {"start": v(-80, -80) * mm, "mid": v(-77.07, -87.07) * mm, "end": v(-70, -90) * mm});
            skLineSegment(sketch, "E79.5", {"start": v(-70, -90) * mm, "end": v(70, -90) * mm});
            skArc(sketch, "E79.6", {"start": v(70, -90) * mm, "mid": v(77.07, -87.07) * mm, "end": v(80, -80) * mm});
            skLineSegment(sketch, "E79.7", {"start": v(80, -80) * mm, "end": v(80, 80) * mm});
            skArc(sketch, "E79.8", {"start": v(80, 80) * mm, "mid": v(77.07, 87.07) * mm, "end": v(70, 90) * mm});
            skCircle(sketch, "E79.9", {"center": v(60, 67.5) * mm, "radius": 4 * mm});
            skCircle(sketch, "E79.10", {"center": v(60, -67.5) * mm, "radius": 4 * mm});
            skCircle(sketch, "E79.11", {"center": v(-60, -67.5) * mm, "radius": 4 * mm});
            skArc(sketch, "E79.12", {"start": v(-56.15, 48.18) * mm, "mid": v(-58.99, 44.68) * mm, "end": v(-60, 40.3) * mm});
            skArc(sketch, "E79.13", {"start": v(56.15, 48.18) * mm, "mid": v(0, 67.5) * mm, "end": v(-56.15, 48.18) * mm});
            skArc(sketch, "E79.14", {"start": v(60, 40.3) * mm, "mid": v(58.99, 44.68) * mm, "end": v(56.15, 48.18) * mm});
            skLineSegment(sketch, "E79.15", {"start": v(60, 40.3) * mm, "end": v(60, -40.3) * mm});
            skArc(sketch, "E79.16", {"start": v(56.15, -48.18) * mm, "mid": v(58.99, -44.68) * mm, "end": v(60, -40.3) * mm});
            skArc(sketch, "E79.17", {"start": v(-56.15, -48.18) * mm, "mid": v(0, -67.5) * mm, "end": v(56.15, -48.18) * mm});
            skLineSegment(sketch, "E79.18", {"start": v(-60, 40.3) * mm, "end": v(-60, -40.3) * mm});
            skArc(sketch, "E79.19", {"start": v(-60, -40.3) * mm, "mid": v(-58.99, -44.68) * mm, "end": v(-56.15, -48.18) * mm});
            skLineSegment(sketch, "E80", {"start": v(0, 90) * mm, "end": v(0, 120) * mm, "construction": true});
            skLineSegment(sketch, "E81", {"start": v(-33, 90) * mm, "end": v(-15, 108) * mm});
            skLineSegment(sketch, "E82", {"start": v(-15, 108) * mm, "end": v(-15, 120) * mm});
            skLineSegment(sketch, "E83", {"start": v(33, 90) * mm, "end": v(15, 108) * mm});
            skLineSegment(sketch, "E84", {"start": v(15, 108) * mm, "end": v(15, 120) * mm});
            skArc(sketch, "E85", {"start": v(15, 120) * mm, "mid": v(0, 135) * mm, "end": v(-15, 120) * mm});
            skCircle(sketch, "E86", {"center": v(0, 120) * mm, "radius": 6 * mm});
            skLineSegment(sketch, "E87", {"start": v(-80, 0) * mm, "end": v(80, 0) * mm, "construction": true});
            skLineSegment(sketch, "E88.MirrorCS", {"start": v(-33, -90) * mm, "end": v(-15, -108) * mm});
            skLineSegment(sketch, "E89.MirrorCS", {"start": v(-15, -108) * mm, "end": v(-15, -120) * mm});
            skArc(sketch, "E90.MirrorCS", {"start": v(15, -120) * mm, "mid": v(0, -135) * mm, "end": v(-15, -120) * mm});
            skLineSegment(sketch, "E91.MirrorCS", {"start": v(33, -90) * mm, "end": v(15, -108) * mm});
            skLineSegment(sketch, "E92.MirrorCS", {"start": v(15, -108) * mm, "end": v(15, -120) * mm});
            skCircle(sketch, "E93.MirrorC", {"center": v(0, -120) * mm, "radius": 6 * mm});
            skSolve(sketch);
        }
        {
            var Q0;
            Q0 = qSketchRegion(id + "F16", true);
            var Q1;
            {var subQ1=sQuery(id+"F16.wireOp",EDGE,"E81");Q1=makeQuery(id+"F16.imprint","IMPRINT",FACE,{"disambiguationData":[TD([[makeQuery(id+"F16.imprint","IMPRINT",EDGE,{"derivedFrom":subQ1}),-1.0]])]});}
            var Q2;
            Q2=makeQuery(id+"F2.opExtrude","CAP_FACE",FACE,{"disambiguationData":[OSD([sQuery(id+"F0.wireOp",EDGE,"E12"),sQuery(id+"F0.wireOp",EDGE,"E13"),sQuery(id+"F0.wireOp",EDGE,"E14"),sQuery(id+"F0.wireOp",EDGE,"E15"),sQuery(id+"F0.wireOp",EDGE,"E17.filletArc"),sQuery(id+"F0.wireOp",EDGE,"E18.filletArc"),sQuery(id+"F0.wireOp",EDGE,"E19.filletArc"),sQuery(id+"F0.wireOp",EDGE,"E20.filletArc"),sQuery(id+"F0.wireOp",EDGE,"E25.0"),sQuery(id+"F0.wireOp",EDGE,"E25.1"),sQuery(id+"F0.wireOp",EDGE,"E25.2"),sQuery(id+"F0.wireOp",EDGE,"E25.3"),sQuery(id+"F0.wireOp",EDGE,"E25.4"),sQuery(id+"F0.wireOp",EDGE,"E25.5"),sQuery(id+"F0.wireOp",EDGE,"E25.6"),sQuery(id+"F0.wireOp",EDGE,"E25.7")])],"isStart":false});
            extrude(context, id + "F17", {"entities" : qUnion([Q0, Q1]), "endBound" : BoundingType.UP_TO_SURFACE, "endBoundEntityFace" : qUnion([Q2]), "depth" : 25 * mm});
        }
    });
